# Revit family: Controller ESP-LXIVM
name_source: partatom
category: Dispositivos de dados
units: mm (PartAtom-declared; Revit-internal decimal feet)

## family parameters
Com base no plano de trabalho = Não
Compartilhado = Não
Corte com vazios quando carregada = Não
Cota do conector redondo = Utilizar diâmetro
Manter orientação da anotação = Não
Número OmniClass = 23.85.50.00
Ponto de cálculo do ambiente = Não
Sempre na vertical = Sim
Tipo de parte = Normal
Título OmniClass = Communication Systems

## types (2) — shared parameters
Corrente de Saída = 2 A
DTT2 = 124
DTT3 = 5  [stored 0.0164042 ft]
Depth = 140  [stored 0.459318 ft]
Elevação padrão = 800  [stored 2.62467 ft]
Heigth = 322  [stored 1.05643 ft]
LXMM = Sim
Power = 11 VA
RainBird: Product Link = www.rainbird.com
Supply = 120 VA
SupportProjetos: Level of Detail = LOD 300
SupportProjetos: Review = R00
Tipo de imagem = <Nenhum>
URL = www.rainbird.com
White = BRANCO
Width = 364  [stored 1.19423 ft]

## per-type parameters (varying)
| type | Descrição | RainBird: Description |
| ESPLXIVM | Controller two LX-IVM files | Controller two LX-IVM files |
| ESPLXIVMP | Controller two LX-IVM PRO files | Controller two LX-IVM PRO files |

note: column(s) folded — value = type name in every type: Modelo

note: [stored X ft] marks values corroborated as IEEE doubles in the binary element streams (Revit-internal decimal feet)
